# Revit family: Faucet-Widespread-American_Standard-Delancey-70528XX_Series
name_source: partatom
category: Plumbing Fixtures
revit_build: Autodesk Revit 2014 (Build: 20130308_1515(x64)
units: mm (PartAtom-declared; Revit-internal decimal feet)

## types (9) — shared parameters
ADA Compliant = Yes
Assembly Code = D2020300
CW Connection = Yes
CWFU = 1.5
Cold Water Connection Diameter = 1/2"
Default Elevation = 0"
Description = Delancey Two-Handle Widespread Lavatory Faucet
Flow Rate = 1.2 gpm (4.5 L/min)
HW Connection = Yes
HWFU = 1.5
Height = 8 5/8"
Hot Water Connection Diameter = 1/2"
Inlet Diameter Connection = 0"
Installation Type = Deck Mounted
Length = 9 3/4"
Manufacturer = American Standard
Price = Prices may vary. Please consult Manufacturer Representative for most up-to-date price list.
URL = http://www.americanstandard-us.com
Vent Connection = No
WFU = 2
Waste Connection = No
Width = 8"

## per-type parameters (varying)
| type | Finish | Handle Type | Material | Pop-Up Drain | Temperature Indicators |
| 7052807.002 | Metal-American Standard-002-Polished Chrome | Handle : 002 Lever | Metal-American Standard-002-Polished Chrome | Yes | No |
| 7052807.295 | Metal-American Standard-295-Brushed Nickel | Handle : 295 Lever | Metal-American Standard-295-Brushed Nickel | Yes | No |
| 7052807.013 | Metal-American Standard-013-Polished Nickel | Handle : 013 Lever | Metal-American Standard-013-Polished Nickel | Yes | No |
| 7052807.278 | Metal-American Standard-278-Legacy Bronze | Handle : 278 Lever | Metal-American Standard-278-Legacy Bronze | Yes | No |
| 7052814.002 | Metal-American Standard-002-Polished Chrome | Handle : 002 Lever | Metal-American Standard-002-Polished Chrome | No | Yes |
| 7052827.002 | Metal-American Standard-002-Polished Chrome | Handle : 002 Cross | Metal-American Standard-002-Polished Chrome | Yes | No |
| 7052827.295 | Metal-American Standard-295-Brushed Nickel | Handle : 295 Cross | Metal-American Standard-295-Brushed Nickel | Yes | No |
| 7052827.013 | Metal-American Standard-013-Polished Nickel | Handle : 013 Cross | Metal-American Standard-013-Polished Nickel | Yes | No |
| 7052827.278 | Metal-American Standard-278-Legacy Bronze | Handle : 278 Cross | Metal-American Standard-278-Legacy Bronze | Yes | No |

note: column(s) folded — value = type name in every type: Model

## geometry (parser evidence)
native form markers: Sweep x4
no freeform markers — native parametric forms only
